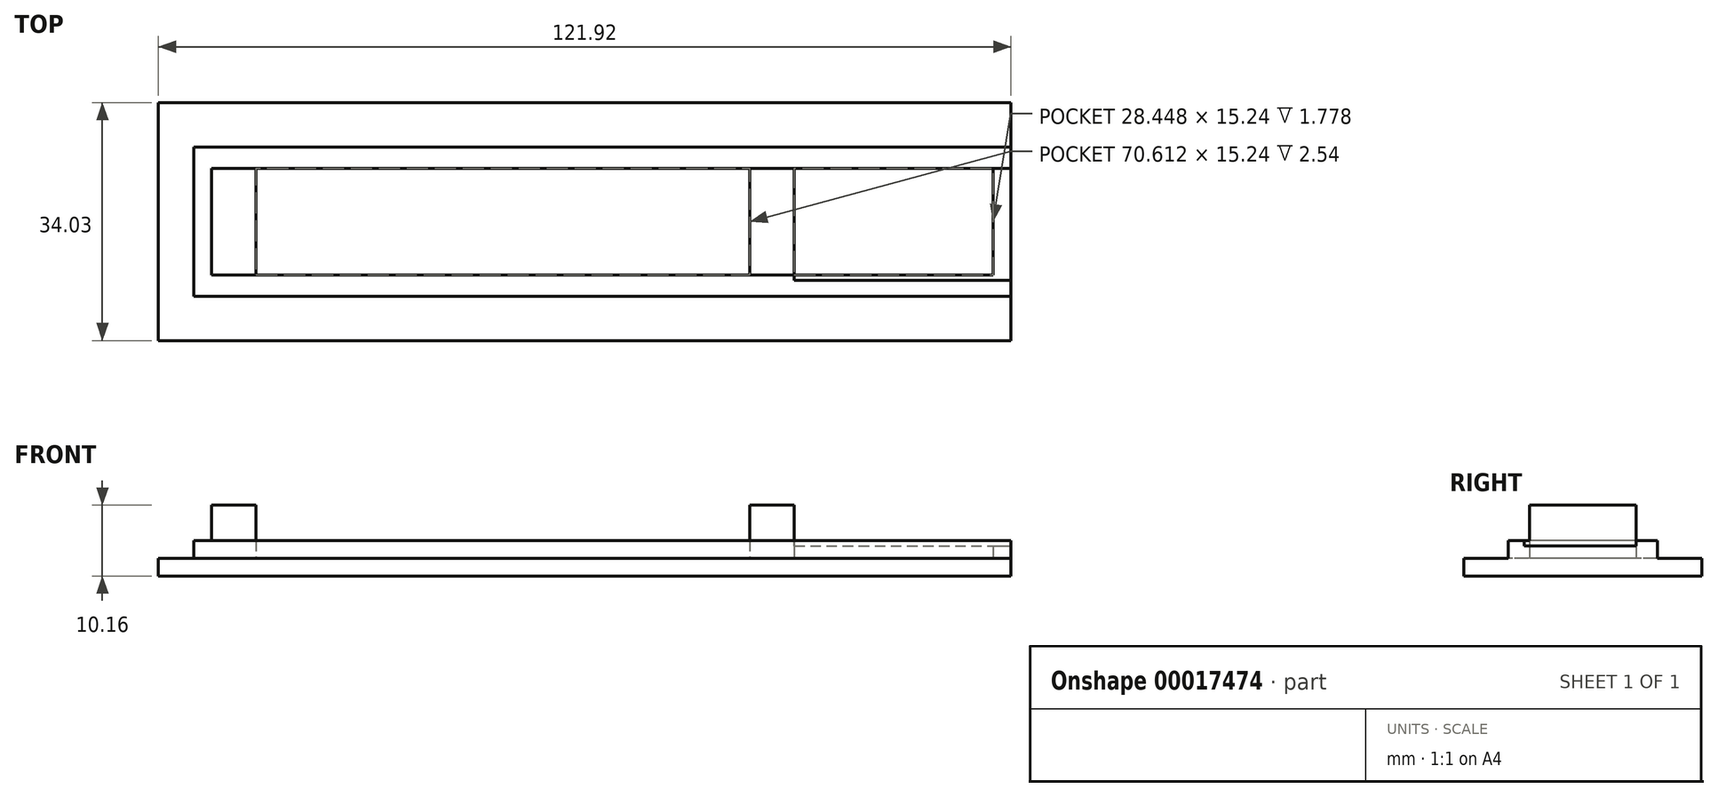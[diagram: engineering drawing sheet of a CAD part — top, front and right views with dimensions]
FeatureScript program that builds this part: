
annotation { "Feature Type Name" : "Feature", "Feature Type Description" : "" }
export const myFeature = defineFeature(function(context is Context, id is Id, definition is map)
    precondition{}
    {
        {
            var Q0;
            Q0=qCreatedBy(makeId("Top.planeOp"),FACE);
            var sketch = newSketch(context, id + "F0", { "sketchPlane" : qUnion([Q0])});
            skLineSegment(sketch, "E0.bottom", {"start": v(-52.87, 3.03) * mm, "end": v(69.05, 3.03) * mm});
            skLineSegment(sketch, "E0.top", {"start": v(-52.87, -31) * mm, "end": v(69.05, -31) * mm});
            skLineSegment(sketch, "E0.left", {"start": v(-52.87, 3.03) * mm, "end": v(-52.87, -31) * mm});
            skLineSegment(sketch, "E0.right", {"start": v(69.05, 3.03) * mm, "end": v(69.05, -31) * mm});
            skSolve(sketch);
        }
        {
            var Q0;
            Q0 = qSketchRegion(id + "F0", true);
            extrude(context, id + "F1", {"entities" : qUnion([Q0]), "depth" : 2.54 * mm});
        }
        {
            var Q0;
            Q0=makeQuery(id+"F1.opExtrude","CAP_FACE",FACE,{"disambiguationData":[OSD([sQuery(id+"F0.wireOp",EDGE,"E0.bottom"),sQuery(id+"F0.wireOp",EDGE,"E0.top"),sQuery(id+"F0.wireOp",EDGE,"E0.left"),sQuery(id+"F0.wireOp",EDGE,"E0.right")])],"isStart":false});
            var sketch = newSketch(context, id + "F2", { "sketchPlane" : qUnion([Q0])});
            skLineSegment(sketch, "E1.bottom", {"start": v(-47.79, -3.32) * mm, "end": v(69.05, -3.32) * mm});
            skLineSegment(sketch, "E1.top", {"start": v(-47.79, -24.65) * mm, "end": v(69.05, -24.65) * mm});
            skLineSegment(sketch, "E1.left", {"start": v(-47.79, -3.32) * mm, "end": v(-47.79, -24.65) * mm});
            skLineSegment(sketch, "E1.right", {"start": v(69.05, -3.32) * mm, "end": v(69.05, -24.65) * mm});
            skSolve(sketch);
        }
        {
            var Q0;
            Q0 = qSketchRegion(id + "F2", true);
            extrude(context, id + "F3", {"entities" : qUnion([Q0]), "operationType" : NewBodyOperationType.ADD, "depth" : 2.54 * mm});
        }
        {
            var Q0;
            Q0=makeQuery(id+"F3.opExtrude","CAP_FACE",FACE,{"disambiguationData":[OSD([sQuery(id+"F2.wireOp",EDGE,"E1.bottom"),sQuery(id+"F2.wireOp",EDGE,"E1.top"),sQuery(id+"F2.wireOp",EDGE,"E1.left"),sQuery(id+"F2.wireOp",EDGE,"E1.right")])],"isStart":false});
            var sketch = newSketch(context, id + "F4", { "sketchPlane" : qUnion([Q0])});
            skLineSegment(sketch, "E2.bottom", {"start": v(-45.25, -6.37) * mm, "end": v(69.05, -6.37) * mm});
            skLineSegment(sketch, "E2.top", {"start": v(-45.25, -21.6) * mm, "end": v(69.05, -21.6) * mm});
            skLineSegment(sketch, "E2.left", {"start": v(-45.25, -6.37) * mm, "end": v(-45.25, -21.6) * mm});
            skLineSegment(sketch, "E2.right", {"start": v(69.05, -6.37) * mm, "end": v(69.05, -21.6) * mm});
            skSolve(sketch);
        }
        {
            var Q0;
            Q0 = qSketchRegion(id + "F4", true);
            extrude(context, id + "F5", {"entities" : qUnion([Q0]), "operationType" : NewBodyOperationType.REMOVE, "oppositeDirection" : true, "depth" : 2.54 * mm});
        }
        {
            var Q0;
            Q0=makeQuery(id+"F1.opExtrude","CAP_FACE",FACE,{"disambiguationData":[OSD([sQuery(id+"F0.wireOp",EDGE,"E0.bottom"),sQuery(id+"F0.wireOp",EDGE,"E0.top"),sQuery(id+"F0.wireOp",EDGE,"E0.left"),sQuery(id+"F0.wireOp",EDGE,"E0.right")])],"isStart":false});
            var sketch = newSketch(context, id + "F6", { "sketchPlane" : qUnion([Q0])});
            skLineSegment(sketch, "E3.bottom", {"start": v(-45.25, -6.37) * mm, "end": v(-38.9, -6.37) * mm});
            skLineSegment(sketch, "E3.top", {"start": v(-45.25, -21.6) * mm, "end": v(-38.9, -21.6) * mm});
            skLineSegment(sketch, "E3.left", {"start": v(-45.25, -6.37) * mm, "end": v(-45.25, -21.6) * mm});
            skLineSegment(sketch, "E3.right", {"start": v(-38.9, -6.37) * mm, "end": v(-38.9, -21.6) * mm});
            skLineSegment(sketch, "E4.bottom", {"start": v(31.71, -6.37) * mm, "end": v(38.06, -6.37) * mm});
            skLineSegment(sketch, "E4.top", {"start": v(31.71, -21.6) * mm, "end": v(38.06, -21.6) * mm});
            skLineSegment(sketch, "E4.left", {"start": v(31.71, -6.37) * mm, "end": v(31.71, -21.6) * mm});
            skLineSegment(sketch, "E4.right", {"start": v(38.06, -6.37) * mm, "end": v(38.06, -21.6) * mm});
            skSolve(sketch);
        }
        {
            var Q0;
            Q0 = qSketchRegion(id + "F6", true);
            extrude(context, id + "F7", {"entities" : qUnion([Q0]), "operationType" : NewBodyOperationType.ADD, "depth" : 7.62 * mm});
        }
        {
            var Q0;
            {var subQ0=sQuery(id+"F4.wireOp",EDGE,"E2.bottom");var subQ1=sQuery(id+"F4.wireOp",EDGE,"E2.top");Q0=makeQuery(id+"F7.boolean.opBoolean","SPLIT",FACE,{"disambiguationData":[TD([makeQuery(id+"F1.opExtrude","SWEPT_FACE",FACE,{"disambiguationData":[OSD([sQuery(id+"F0.wireOp",EDGE,"E0.right")])]})])],"derivedFrom":makeQuery(id+"F5.boolean.opBoolean","COPY",FACE,{"derivedFrom":makeQuery(id+"F5.opExtrude","CAP_FACE",FACE,{"disambiguationData":[OSD([subQ0,subQ1,sQuery(id+"F4.wireOp",EDGE,"E2.left"),sQuery(id+"F4.wireOp",EDGE,"E2.right")])],"isStart":false})})});}
            var sketch = newSketch(context, id + "F8", { "sketchPlane" : qUnion([Q0])});
            skLineSegment(sketch, "E5.bottom", {"start": v(66.51, -6.37) * mm, "end": v(69.05, -6.37) * mm});
            skLineSegment(sketch, "E5.top", {"start": v(66.51, -21.6) * mm, "end": v(69.05, -21.6) * mm});
            skLineSegment(sketch, "E5.left", {"start": v(66.51, -6.37) * mm, "end": v(66.51, -21.6) * mm});
            skLineSegment(sketch, "E5.right", {"start": v(69.05, -6.37) * mm, "end": v(69.05, -21.6) * mm});
            skSolve(sketch);
        }
        {
            var Q0;
            Q0 = qSketchRegion(id + "F8", true);
            extrude(context, id + "F9", {"entities" : qUnion([Q0]), "operationType" : NewBodyOperationType.ADD, "depth" : 1.78 * mm});
        }
        {
            var Q0;
            Q0=makeQuery(id+"F3.opExtrude","CAP_FACE",FACE,{"disambiguationData":[OSD([sQuery(id+"F2.wireOp",EDGE,"E1.bottom"),sQuery(id+"F2.wireOp",EDGE,"E1.top"),sQuery(id+"F2.wireOp",EDGE,"E1.left"),sQuery(id+"F2.wireOp",EDGE,"E1.right")])],"isStart":false});
            var sketch = newSketch(context, id + "F10", { "sketchPlane" : qUnion([Q0])});
            skLineSegment(sketch, "E6.bottom", {"start": v(38.06, -21.6) * mm, "end": v(69.05, -21.6) * mm});
            skLineSegment(sketch, "E6.top", {"start": v(38.06, -22.37) * mm, "end": v(69.05, -22.37) * mm});
            skLineSegment(sketch, "E6.left", {"start": v(38.06, -21.6) * mm, "end": v(38.06, -22.37) * mm});
            skLineSegment(sketch, "E6.right", {"start": v(69.05, -21.6) * mm, "end": v(69.05, -22.37) * mm});
            skSolve(sketch);
        }
        {
            var Q0;
            Q0 = qSketchRegion(id + "F10", true);
            extrude(context, id + "F11", {"entities" : qUnion([Q0]), "operationType" : NewBodyOperationType.REMOVE, "oppositeDirection" : true, "depth" : 0.76 * mm});
        }
    });
